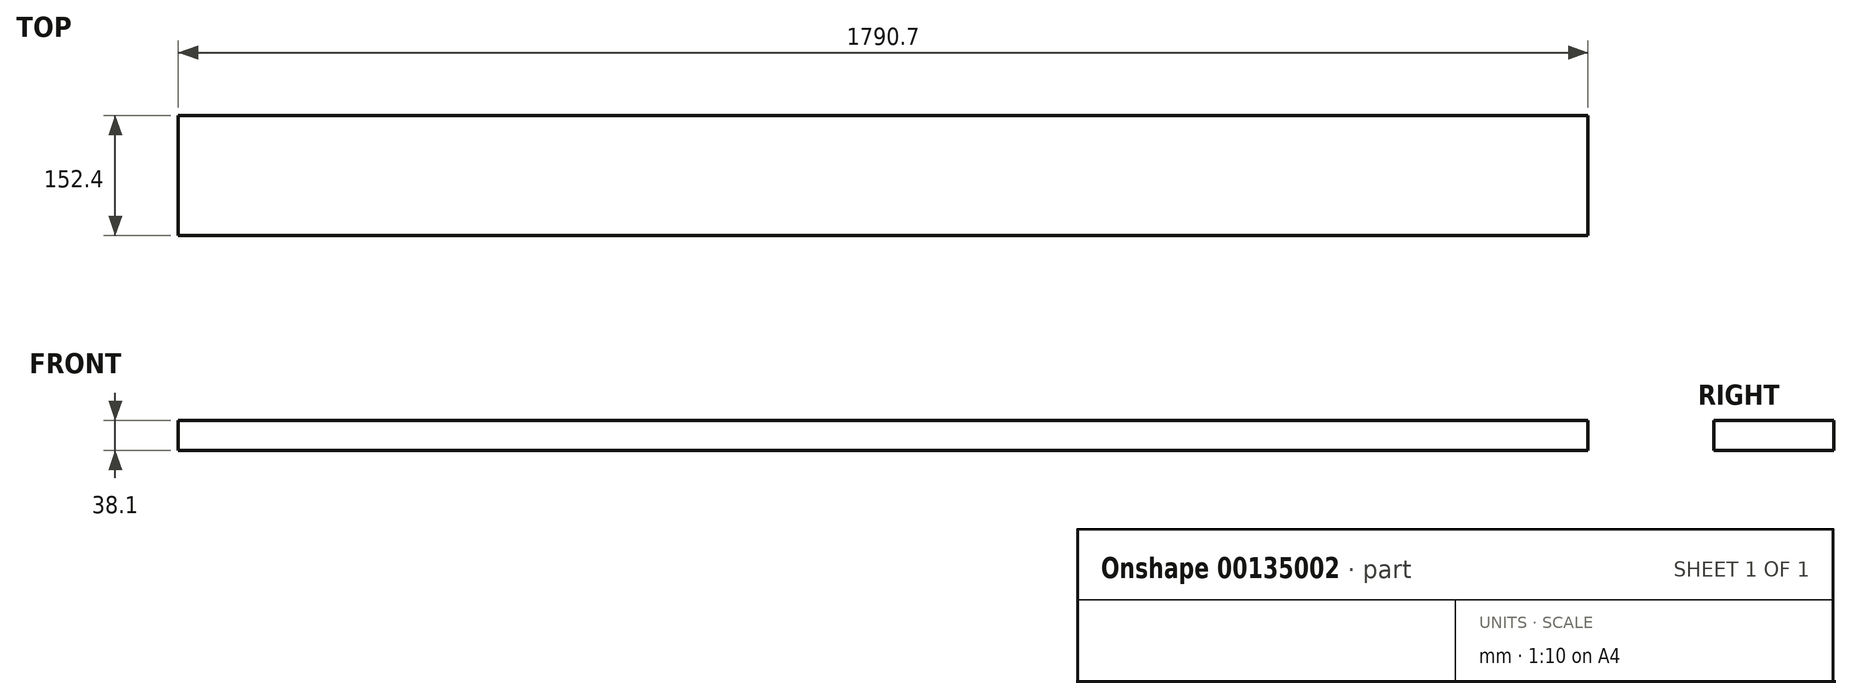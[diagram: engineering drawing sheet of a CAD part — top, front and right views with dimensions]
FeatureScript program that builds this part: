
annotation { "Feature Type Name" : "Feature", "Feature Type Description" : "" }
export const myFeature = defineFeature(function(context is Context, id is Id, definition is map)
    precondition{}
    {
        {
            var Q0;
            Q0=qCreatedBy(makeId("Right.planeOp"),FACE);
            var sketch = newSketch(context, id + "F0", { "sketchPlane" : qUnion([Q0])});
            skLineSegment(sketch, "E0.bottom", {"start": v(0, 0) * mm, "end": v(152.4, 0) * mm});
            skLineSegment(sketch, "E0.top", {"start": v(0, 38.1) * mm, "end": v(152.4, 38.1) * mm});
            skLineSegment(sketch, "E0.left", {"start": v(0, 0) * mm, "end": v(0, 38.1) * mm});
            skLineSegment(sketch, "E0.right", {"start": v(152.4, 0) * mm, "end": v(152.4, 38.1) * mm});
            skSolve(sketch);
        }
        {
            var Q0;
            Q0=makeQuery(id+"F0.imprint","IMPRINT",FACE,{"disambiguationData":[TD([[makeQuery(id+"F0.imprint","IMPRINT",EDGE,{"derivedFrom":sQuery(id+"F0.wireOp",EDGE,"E0.bottom")}),1.0]])]});
            extrude(context, id + "F1", {"entities" : qUnion([Q0]), "depth" : 1790.7 * mm});
        }
    });
